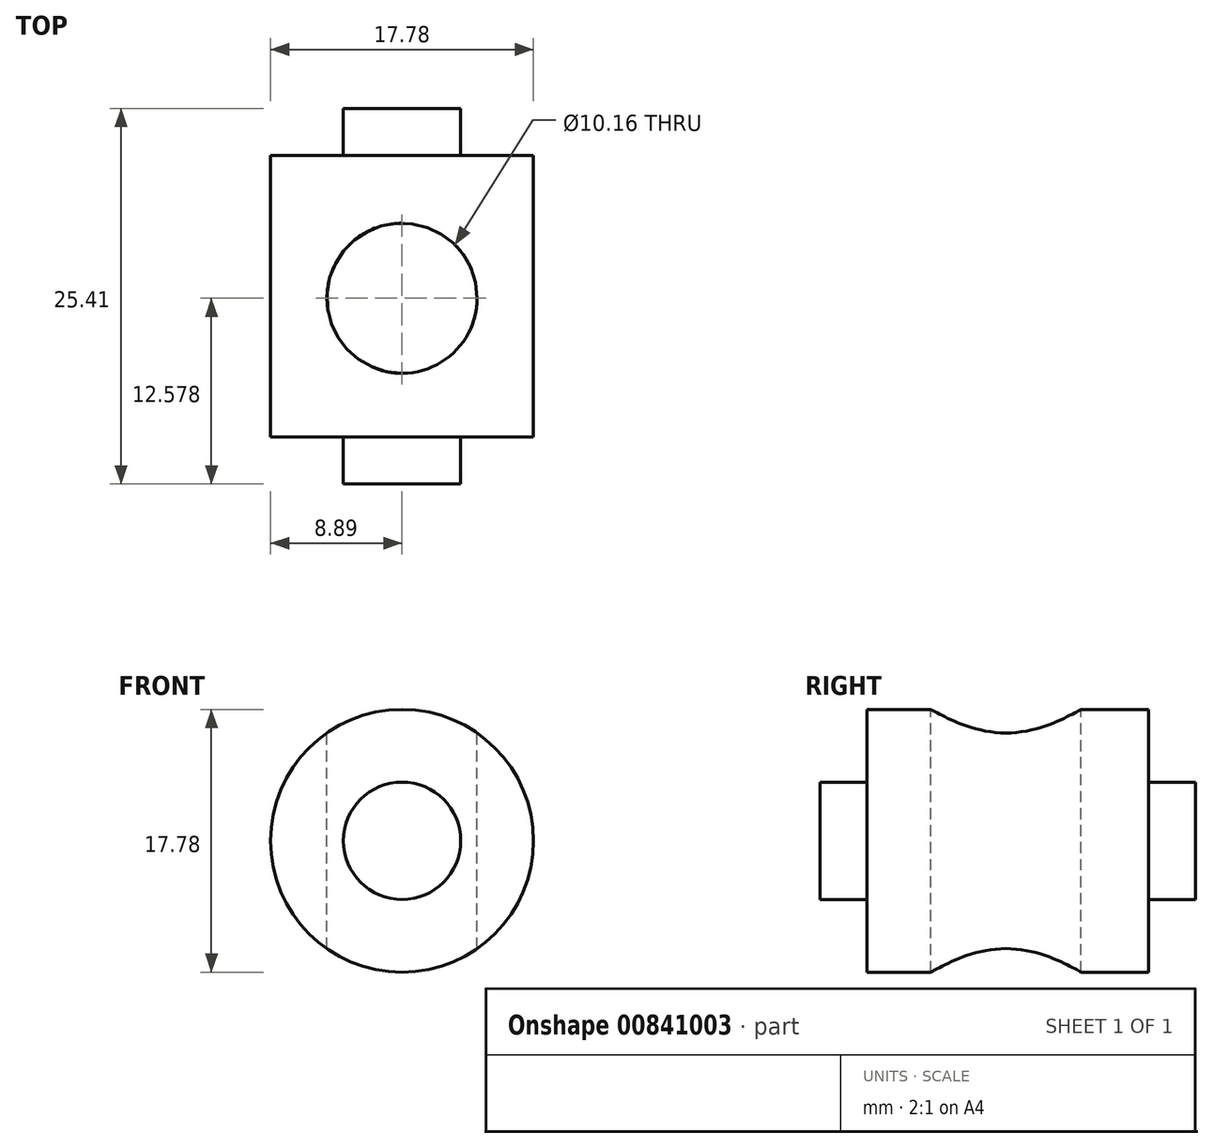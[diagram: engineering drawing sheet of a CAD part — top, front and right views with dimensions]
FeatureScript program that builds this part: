
annotation { "Feature Type Name" : "Feature", "Feature Type Description" : "" }
export const myFeature = defineFeature(function(context is Context, id is Id, definition is map)
    precondition{}
    {
        {
            var Q0;
            Q0=qCreatedBy(makeId("Front.planeOp"),FACE);
            var sketch = newSketch(context, id + "F0", { "sketchPlane" : qUnion([Q0])});
            skCircle(sketch, "E0", {"center": v(0, 0) * mm, "radius": 8.9 * mm});
            skSolve(sketch);
        }
        {
            var Q0;
            Q0 = qSketchRegion(id + "F0", true);
            extrude(context, id + "F1", {"entities" : qUnion([Q0]), "depth" : 19.05 * mm, "offsetDistance" : 25.4 * mm});
        }
        {
            var Q0;
            Q0=makeQuery(id+"F1.opExtrude","CAP_FACE",FACE,{"disambiguationData":[OSD([sQuery(id+"F0.wireOp",EDGE,"E0")])],"isStart":false});
            var sketch = newSketch(context, id + "F2", { "sketchPlane" : qUnion([Q0])});
            skCircle(sketch, "E1", {"center": v(0, 0) * mm, "radius": 3.97 * mm});
            skSolve(sketch);
        }
        {
            var Q0;
            Q0 = qSketchRegion(id + "F2", true);
            extrude(context, id + "F3", {"entities" : qUnion([Q0]), "operationType" : NewBodyOperationType.ADD, "depth" : 3.17 * mm, "offsetDistance" : 25.4 * mm});
        }
        {
            var Q0;
            Q0=makeQuery(id+"F1.opExtrude","CAP_FACE",FACE,{"disambiguationData":[OSD([sQuery(id+"F0.wireOp",EDGE,"E0")])],"isStart":true});
            var sketch = newSketch(context, id + "F4", { "sketchPlane" : qUnion([Q0])});
            skCircle(sketch, "E2", {"center": v(0, 0) * mm, "radius": 3.97 * mm});
            skSolve(sketch);
        }
        {
            var Q0;
            Q0 = qSketchRegion(id + "F4", true);
            extrude(context, id + "F5", {"entities" : qUnion([Q0]), "operationType" : NewBodyOperationType.ADD, "depth" : 3.17 * mm, "offsetDistance" : 25.4 * mm});
        }
        {
            var Q0;
            Q0=qCreatedBy(makeId("Top.planeOp"),FACE);
            cPlane(context, id + "F6", {"entities" : qUnion([Q0]), "cplaneType" : CPlaneType.OFFSET, "offset" : 10.16 * mm, "width" : 152.4 * mm, "height" : 152.4 * mm});
        }
        {
            var Q0;
            Q0=qCreatedBy(id+"F6.planeOp",FACE);
            var sketch = newSketch(context, id + "F7", { "sketchPlane" : qUnion([Q0])});
            skCircle(sketch, "E3", {"center": v(0, -9.65) * mm, "radius": 5.08 * mm});
            skSolve(sketch);
        }
        {
            var Q0;
            Q0 = qSketchRegion(id + "F7", true);
            extrude(context, id + "F8", {"entities" : qUnion([Q0]), "operationType" : NewBodyOperationType.REMOVE, "oppositeDirection" : true, "depth" : 25.4 * mm, "offsetDistance" : 25.4 * mm});
        }
    });
